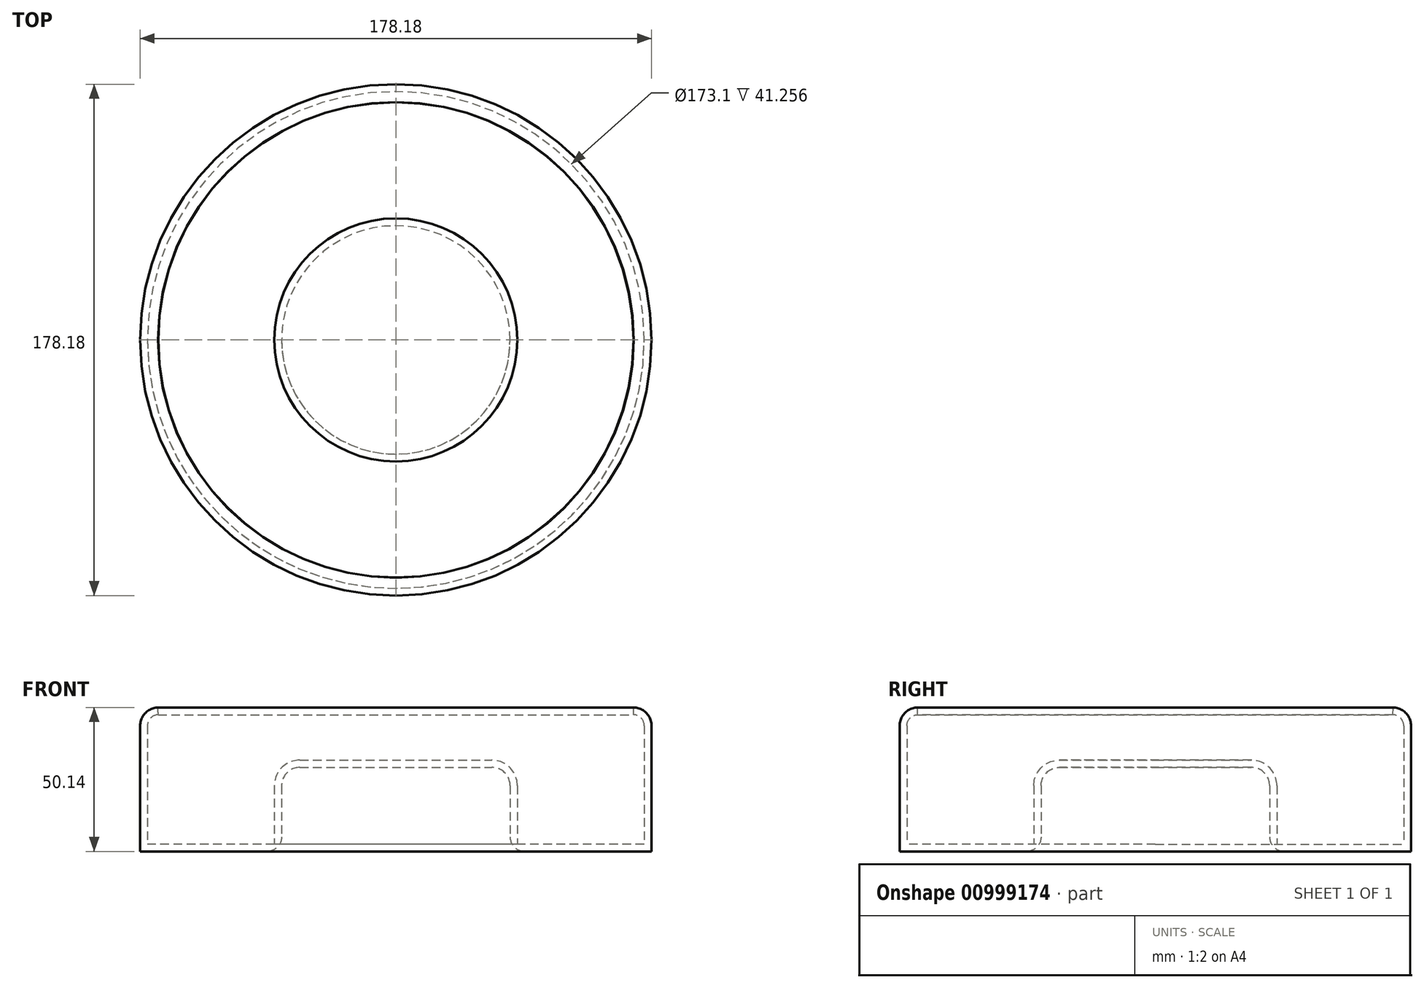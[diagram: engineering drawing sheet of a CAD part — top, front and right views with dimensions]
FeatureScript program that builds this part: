
annotation { "Feature Type Name" : "Feature", "Feature Type Description" : "" }
export const myFeature = defineFeature(function(context is Context, id is Id, definition is map)
    precondition{}
    {
        {
            var Q0;
            Q0=qCreatedBy(makeId("Front.planeOp"),FACE);
            var sketch = newSketch(context, id + "F0", { "sketchPlane" : qUnion([Q0])});
            skLineSegment(sketch, "E0", {"start": v(-64.21, 53.66) * mm, "end": v(-64.21, 9.86) * mm});
            skLineSegment(sketch, "E1", {"start": v(-64.21, 9.86) * mm, "end": v(-14.93, 9.86) * mm});
            skLineSegment(sketch, "E2", {"start": v(-14.93, 9.86) * mm, "end": v(-14.93, 32.77) * mm});
            skLineSegment(sketch, "E3", {"start": v(-8.58, 39.12) * mm, "end": v(24.88, 39.12) * mm});
            skLineSegment(sketch, "E4", {"start": v(24.88, 39.12) * mm, "end": v(24.88, 61.51) * mm});
            skLineSegment(sketch, "E5", {"start": v(24.88, 61.51) * mm, "end": v(-57.98, 60) * mm});
            skPoint(sketch, "E6.visualSharp", {"position": v(-64.21, 59.9) * mm});
            skArc(sketch, "E6.filletArc", {"start": v(-57.98, 60) * mm, "mid": v(-62.4, 58.1) * mm, "end": v(-64.21, 53.66) * mm});
            skPoint(sketch, "E7.visualSharp", {"position": v(-14.93, 39.12) * mm});
            skArc(sketch, "E7.filletArc", {"start": v(-8.58, 39.12) * mm, "mid": v(-13.07, 37.26) * mm, "end": v(-14.93, 32.77) * mm});
            skSolve(sketch);
        }
        {
            var Q0;
            Q0=makeQuery(id+"F0.imprint","IMPRINT",FACE,{"disambiguationData":[TD([[makeQuery(id+"F0.imprint","IMPRINT",EDGE,{"derivedFrom":sQuery(id+"F0.wireOp",EDGE,"E0")}),1.0]])]});
            var Q1;
            Q1=sQuery(id+"F0.wireOp",EDGE,"E4");
            revolve(context, id + "F1", {"surfaceOperationType" : NewSurfaceOperationType.NEW, "entities" : qUnion([Q0]), "axis" : qUnion([Q1]), "revolveType" : RevolveType.FULL});
        }
        {
            var Q0;
            Q0=makeQuery(id+"F1.opRevolve","SWEPT_FACE",FACE,{"disambiguationData":[OSD([sQuery(id+"F0.wireOp",EDGE,"E5")])]});
            shell(context, id + "F2", {"entities" : qUnion([Q0]), "thickness" : 2.54 * mm});
        }
        {
            var Q0;
            Q0=makeQuery(id+"F1.opRevolve","SWEPT_EDGE",EDGE,{"disambiguationData":[OSD([sQuery(id+"F0.wireOp",EDGE,"E1"),sQuery(id+"F0.wireOp",EDGE,"E2")])]});
            fillet(context, id + "F3", {"entities" : qUnion([Q0]), "radius" : 5.08 * mm, "tangentPropagation" : true, "allowEdgeOverflow" : false});
        }
    });
